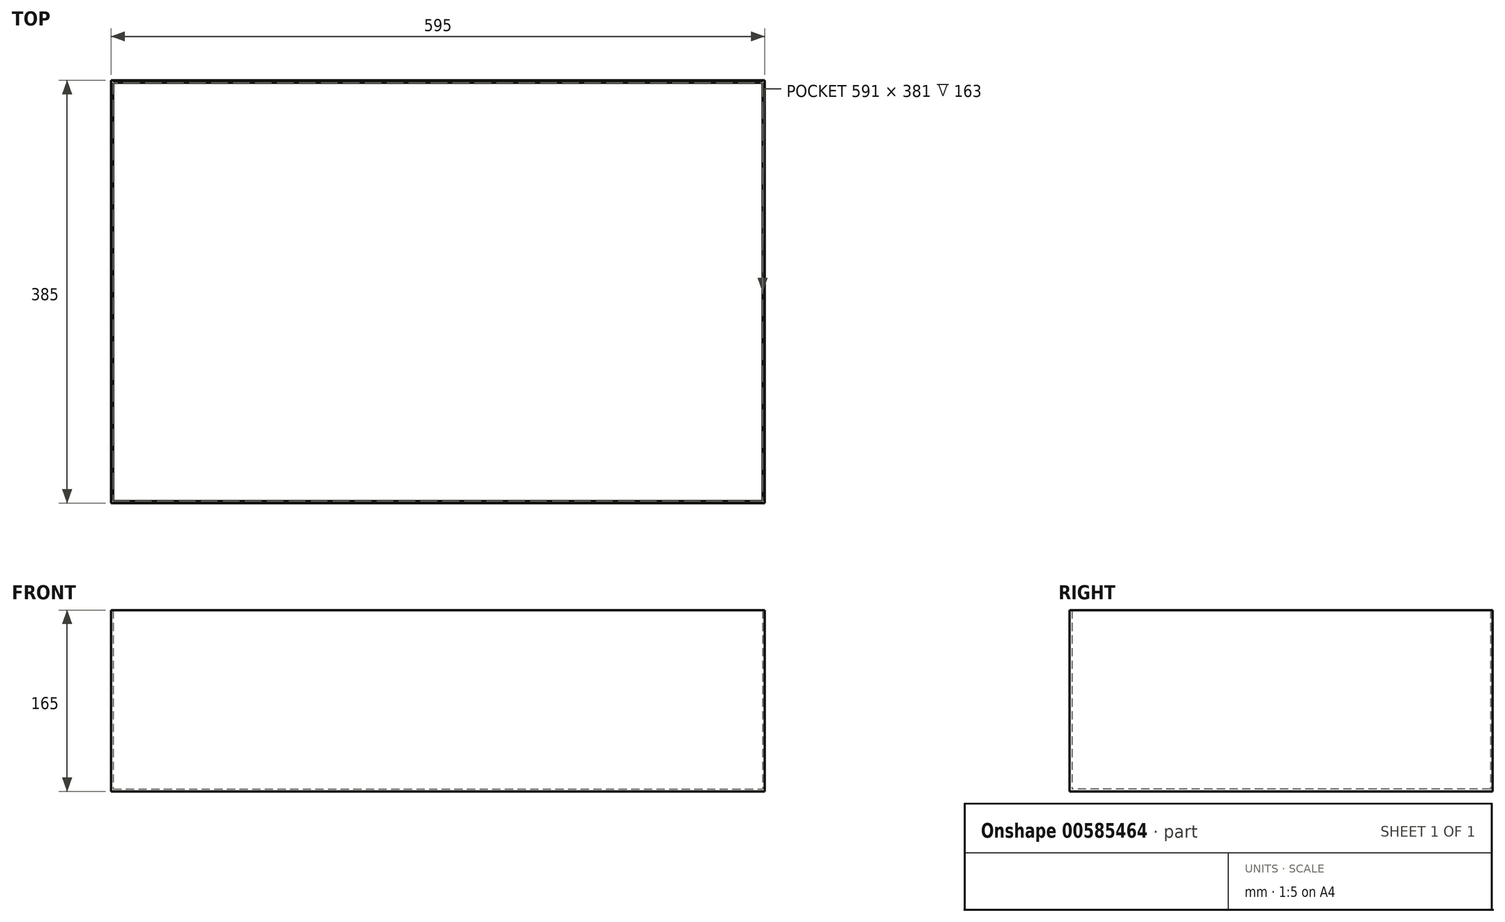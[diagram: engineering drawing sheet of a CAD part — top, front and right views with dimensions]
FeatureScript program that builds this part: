
annotation { "Feature Type Name" : "Feature", "Feature Type Description" : "" }
export const myFeature = defineFeature(function(context is Context, id is Id, definition is map)
    precondition{}
    {
        {
            assignVariable(context, id + "F0", {"name" : "BT", "anyValue" : 2 * mm});
        }
        {
            var Q0;
            Q0=qCreatedBy(makeId("Top.planeOp"),FACE);
            var sketch = newSketch(context, id + "F1", { "sketchPlane" : qUnion([Q0])});
            skLineSegment(sketch, "E0.bottom", {"start": v(0, 0) * mm, "end": v(595, 0) * mm});
            skLineSegment(sketch, "E0.top", {"start": v(0, -385) * mm, "end": v(595, -385) * mm});
            skLineSegment(sketch, "E0.left", {"start": v(0, 0) * mm, "end": v(0, -385) * mm});
            skLineSegment(sketch, "E0.right", {"start": v(595, 0) * mm, "end": v(595, -385) * mm});
            skSolve(sketch);
        }
        {
            var Q0;
            Q0=makeQuery(id+"F1.imprint","IMPRINT",FACE,{"disambiguationData":[TD([[makeQuery(id+"F1.imprint","IMPRINT",EDGE,{"derivedFrom":sQuery(id+"F1.wireOp",EDGE,"E0.bottom")}),-1.0]])]});
            extrude(context, id + "F2", {"entities" : qUnion([Q0]), "depth" : getVariable(context, 'BT'), "offsetDistance" : 25 * mm});
        }
        {
            var Q0;
            Q0=makeQuery(id+"F2.opExtrude","CAP_FACE",FACE,{"disambiguationData":[OSD([sQuery(id+"F1.wireOp",EDGE,"E0.bottom"),sQuery(id+"F1.wireOp",EDGE,"E0.top"),sQuery(id+"F1.wireOp",EDGE,"E0.left"),sQuery(id+"F1.wireOp",EDGE,"E0.right")])],"isStart":false});
            var sketch = newSketch(context, id + "F3", { "sketchPlane" : qUnion([Q0])});
            skLineSegment(sketch, "E1.bottom", {"start": v(0, 0) * mm, "end": v(595, 0) * mm});
            skLineSegment(sketch, "E1.top", {"start": v(0, -385) * mm, "end": v(595, -385) * mm});
            skLineSegment(sketch, "E1.left", {"start": v(0, 0) * mm, "end": v(0, -385) * mm});
            skLineSegment(sketch, "E1.right", {"start": v(595, 0) * mm, "end": v(595, -385) * mm});
            skLineSegment(sketch, "E2.bottom", {"start": v(2, -2) * mm, "end": v(593, -2) * mm});
            skLineSegment(sketch, "E2.top", {"start": v(2, -383) * mm, "end": v(593, -383) * mm});
            skLineSegment(sketch, "E2.left", {"start": v(2, -2) * mm, "end": v(2, -383) * mm});
            skLineSegment(sketch, "E2.right", {"start": v(593, -2) * mm, "end": v(593, -383) * mm});
            skSolve(sketch);
        }
        {
            var Q0;
            Q0=makeQuery(id+"F3.imprint","IMPRINT",FACE,{"disambiguationData":[TD([[makeQuery(id+"F3.imprint","IMPRINT",EDGE,{"derivedFrom":sQuery(id+"F3.wireOp",EDGE,"E1.bottom")}),-1.0]])]});
            extrude(context, id + "F4", {"entities" : qUnion([Q0]), "operationType" : NewBodyOperationType.ADD, "depth" : 163 * mm, "offsetDistance" : 25 * mm});
        }
    });
